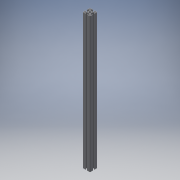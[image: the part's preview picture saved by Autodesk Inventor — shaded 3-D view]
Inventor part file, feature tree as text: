
AUTODESK INVENTOR PART (.ipt)
format: ipt  version: 2018 (Build 220112000, 112)  size: 202,240 bytes
history: native  units: mm
features: other x42, sketch x5, hole x4, extrude x1
ambient origin geometry x8: Origin, YZ Plane, XZ Plane, XY Plane, X Axis, Y Axis, Z Axis, Center Point
bodies: Solid1 (feature_tree)
feature tree (52):
  extrude  "Extrusion1"  [1 undecoded]
  hole  "Drilling 1"  [1 undecoded]
  hole  "Drilling 2"  [1 undecoded]
  hole  "Drilling 3"  [1 undecoded]
  hole  "Drilling 4"  [1 undecoded]
  other  "side_4d_XY"
  other  "side_4d_YZ"
  other  "side_4d_ZX"
  other  "side_4d_X"
  other  "side_4d_Y"
  other  "side_4d_Z"
  other  "side_4d_Center"
  other  "side_1a_XY"
  other  "side_1a_YZ"
  other  "side_1a_ZX"
  other  "side_1a_X"
  other  "side_1a_Y"
  other  "side_1a_Z"
  other  "side_1a_Center"
  other  "side_2b_XY"
  other  "side_2b_YZ"
  other  "side_2b_ZX"
  other  "side_2b_X"
  other  "side_2b_Y"
  other  "side_2b_Z"
  other  "side_2b_Center"
  other  "side_3c_XY"
  other  "side_3c_YZ"
  other  "side_3c_ZX"
  other  "side_3c_X"
  other  "side_3c_Y"
  other  "side_3c_Z"
  other  "side_3c_Center"
  other  "end_XY"
  other  "end_YZ"
  other  "end_ZX"
  other  "end_X"
  other  "end_Y"
  other  "end_Z"
  other  "end_Center"
  other  "start_XY"
  other  "start_YZ"
  other  "start_ZX"
  other  "start_X"
  other  "start_Y"
  other  "start_Z"
  other  "start_Center"
  sketch  "Skizze_1"  dims[d0=740.0mm d1=0.0mm]
  sketch  "Sketch2"  dims[d2=5.0mm d3=6.0mm d4=4.0mm d5=2.0mm d6=90.0deg d7=6000.0mm d8=0.0mm]
  sketch  "Sketch3"  dims[d9=5.0mm d10=6.0mm d11=4.0mm d12=2.0mm d13=90.0deg d14=6000.0mm d15=0.0mm]
  sketch  "Sketch4"  dims[d16=5.0mm d17=6.0mm d18=4.0mm d19=2.0mm d20=90.0deg d21=6000.0mm d22=0.0mm]
  sketch  "Sketch5"  dims[d23=5.0mm d24=6.0mm d25=4.0mm d26=2.0mm d27=90.0deg d28=6000.0mm d29=0.0mm]
note: 5 required parameter values undecoded (feature->parameter linkage not recoverable at this tier; creation-order binding heuristic only, values carry confidence <= 0.55)
